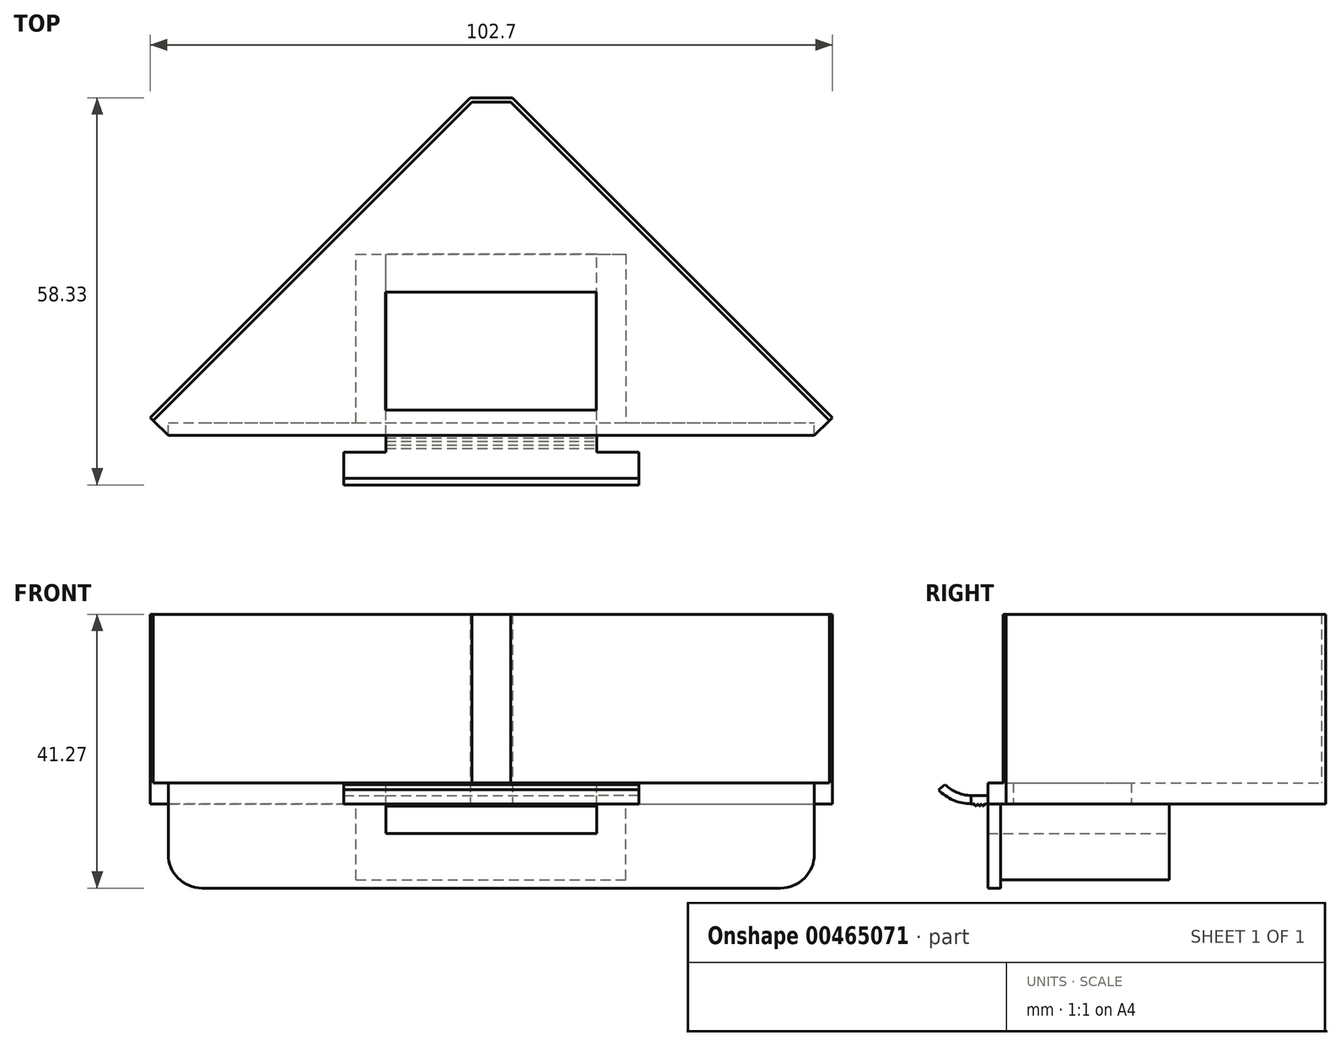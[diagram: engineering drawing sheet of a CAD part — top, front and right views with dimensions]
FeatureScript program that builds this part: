
annotation { "Feature Type Name" : "Feature", "Feature Type Description" : "" }
export const myFeature = defineFeature(function(context is Context, id is Id, definition is map)
    precondition{}
    {
        {
            var Q0;
            Q0=qCreatedBy(makeId("Top.planeOp"),FACE);
            var sketch = newSketch(context, id + "F0", { "sketchPlane" : qUnion([Q0])});
            skLineSegment(sketch, "E0", {"start": v(-3.17, 48.17) * mm, "end": v(-51.35, 0) * mm});
            skLineSegment(sketch, "E1", {"start": v(3.17, 48.17) * mm, "end": v(51.35, 0) * mm});
            skLineSegment(sketch, "E2", {"start": v(-51.35, 0) * mm, "end": v(51.35, 0) * mm, "construction": true});
            skLineSegment(sketch, "E3", {"start": v(3.17, 48.17) * mm, "end": v(-3.17, 48.17) * mm});
            skPoint(sketch, "E4.endSnap0", {"position": v(0, 0) * mm});
            skLineSegment(sketch, "E5", {"start": v(0, 0) * mm, "end": v(0, 48.17) * mm, "construction": true});
            skLineSegment(sketch, "E6", {"start": v(51.35, 0) * mm, "end": v(48.65, -2.7) * mm});
            skLineSegment(sketch, "E7", {"start": v(-51.35, 0) * mm, "end": v(-48.65, -2.7) * mm});
            skLineSegment(sketch, "E8", {"start": v(48.65, -2.7) * mm, "end": v(-48.65, -2.7) * mm});
            skSolve(sketch);
        }
        {
            var Q0;
            Q0=makeQuery(id+"F0.imprint","IMPRINT",FACE,{"disambiguationData":[TD([[makeQuery(id+"F0.imprint","IMPRINT",EDGE,{"derivedFrom":sQuery(id+"F0.wireOp",EDGE,"E0")}),1.0]])]});
            extrude(context, id + "F1", {"entities" : qUnion([Q0]), "depth" : 3.17 * mm, "offsetDistance" : 25.4 * mm});
        }
        {
            var Q0;
            Q0=makeQuery(id+"F1.opExtrude","CAP_FACE",FACE,{"disambiguationData":[OSD([sQuery(id+"F0.wireOp",EDGE,"E0"),sQuery(id+"F0.wireOp",EDGE,"E1"),sQuery(id+"F0.wireOp",EDGE,"E3"),sQuery(id+"F0.wireOp",EDGE,"E6"),sQuery(id+"F0.wireOp",EDGE,"E7"),sQuery(id+"F0.wireOp",EDGE,"E8")])],"isStart":false});
            var sketch = newSketch(context, id + "F2", { "sketchPlane" : qUnion([Q0])});
            skLineSegment(sketch, "E9", {"start": v(-51.35, 0) * mm, "end": v(-3.17, 48.17) * mm});
            skLineSegment(sketch, "E10", {"start": v(-3.17, 48.17) * mm, "end": v(3.17, 48.17) * mm});
            skLineSegment(sketch, "E11", {"start": v(3.17, 48.17) * mm, "end": v(51.35, 0) * mm});
            skLineSegment(sketch, "E12", {"start": v(51.35, 0) * mm, "end": v(50.9, -0.45) * mm});
            skLineSegment(sketch, "E13", {"start": v(-51.35, 0) * mm, "end": v(-50.9, -0.45) * mm});
            skLineSegment(sketch, "E14", {"start": v(-50.9, -0.45) * mm, "end": v(-2.92, 47.53) * mm});
            skLineSegment(sketch, "E15", {"start": v(50.9, -0.45) * mm, "end": v(2.92, 47.53) * mm});
            skLineSegment(sketch, "E16", {"start": v(-2.92, 47.53) * mm, "end": v(2.92, 47.53) * mm});
            skSolve(sketch);
        }
        {
            var Q0;
            Q0=makeQuery(id+"F2.imprint","IMPRINT",FACE,{"disambiguationData":[TD([[makeQuery(id+"F2.imprint","IMPRINT",EDGE,{"derivedFrom":sQuery(id+"F2.wireOp",EDGE,"E9")}),1.0]])]});
            extrude(context, id + "F3", {"entities" : qUnion([Q0]), "operationType" : NewBodyOperationType.ADD, "depth" : 25.4 * mm, "offsetDistance" : 25.4 * mm});
        }
        {
            var Q0;
            Q0=makeQuery(id+"F1.opExtrude","CAP_FACE",FACE,{"disambiguationData":[OSD([sQuery(id+"F0.wireOp",EDGE,"E0"),sQuery(id+"F0.wireOp",EDGE,"E1"),sQuery(id+"F0.wireOp",EDGE,"E3"),sQuery(id+"F0.wireOp",EDGE,"E6"),sQuery(id+"F0.wireOp",EDGE,"E7"),sQuery(id+"F0.wireOp",EDGE,"E8")])],"isStart":true});
            var sketch = newSketch(context, id + "F4", { "sketchPlane" : qUnion([Q0])});
            skLineSegment(sketch, "E17", {"start": v(-48.65, 2.7) * mm, "end": v(48.65, 2.7) * mm});
            skLineSegment(sketch, "E18", {"start": v(48.65, 2.7) * mm, "end": v(48.65, 0.79) * mm});
            skLineSegment(sketch, "E19", {"start": v(-48.65, 2.7) * mm, "end": v(-48.65, 0.79) * mm});
            skLineSegment(sketch, "E20", {"start": v(-48.65, 0.79) * mm, "end": v(48.65, 0.79) * mm});
            skSolve(sketch);
        }
        {
            var Q0;
            Q0=makeQuery(id+"F4.imprint","IMPRINT",FACE,{"disambiguationData":[TD([[makeQuery(id+"F4.imprint","IMPRINT",EDGE,{"derivedFrom":sQuery(id+"F4.wireOp",EDGE,"E17")}),1.0]])]});
            extrude(context, id + "F5", {"entities" : qUnion([Q0]), "operationType" : NewBodyOperationType.ADD, "depth" : 12.7 * mm, "offsetDistance" : 25.4 * mm});
        }
        {
            var Q0;
            Q0=makeQuery(id+"F1.opExtrude","CAP_FACE",FACE,{"disambiguationData":[OSD([sQuery(id+"F0.wireOp",EDGE,"E0"),sQuery(id+"F0.wireOp",EDGE,"E1"),sQuery(id+"F0.wireOp",EDGE,"E3"),sQuery(id+"F0.wireOp",EDGE,"E6"),sQuery(id+"F0.wireOp",EDGE,"E7"),sQuery(id+"F0.wireOp",EDGE,"E8")])],"isStart":true});
            var sketch = newSketch(context, id + "F6", { "sketchPlane" : qUnion([Q0])});
            skLineSegment(sketch, "E21", {"start": v(-20.36, 0.79) * mm, "end": v(-20.36, -24.61) * mm});
            skLineSegment(sketch, "E22", {"start": v(-20.36, -24.61) * mm, "end": v(20.28, -24.61) * mm});
            skLineSegment(sketch, "E23", {"start": v(20.28, -24.61) * mm, "end": v(20.28, 0.79) * mm});
            skLineSegment(sketch, "E24", {"start": v(20.28, 0.79) * mm, "end": v(-20.36, 0.79) * mm});
            skSolve(sketch);
        }
        {
            var Q0;
            Q0=makeQuery(id+"F6.imprint","IMPRINT",FACE,{"disambiguationData":[TD([[makeQuery(id+"F6.imprint","IMPRINT",EDGE,{"derivedFrom":sQuery(id+"F6.wireOp",EDGE,"E21")}),1.0]])]});
            extrude(context, id + "F7", {"entities" : qUnion([Q0]), "operationType" : NewBodyOperationType.ADD, "depth" : 11.43 * mm, "offsetDistance" : 25.4 * mm});
        }
        {
            var Q0;
            Q0=makeQuery(id+"F1.opExtrude","CAP_FACE",FACE,{"disambiguationData":[OSD([sQuery(id+"F0.wireOp",EDGE,"E0"),sQuery(id+"F0.wireOp",EDGE,"E1"),sQuery(id+"F0.wireOp",EDGE,"E3"),sQuery(id+"F0.wireOp",EDGE,"E6"),sQuery(id+"F0.wireOp",EDGE,"E7"),sQuery(id+"F0.wireOp",EDGE,"E8")])],"isStart":true});
            var sketch = newSketch(context, id + "F8", { "sketchPlane" : qUnion([Q0])});
            skLineSegment(sketch, "E25", {"start": v(15.84, -1.12) * mm, "end": v(-15.91, -1.12) * mm});
            skLineSegment(sketch, "E26", {"start": v(15.84, -1.12) * mm, "end": v(15.84, -18.9) * mm});
            skLineSegment(sketch, "E27", {"start": v(-15.91, -1.12) * mm, "end": v(-15.91, -18.9) * mm});
            skLineSegment(sketch, "E28", {"start": v(15.84, -18.9) * mm, "end": v(-15.91, -18.9) * mm});
            skSolve(sketch);
        }
        {
            var Q0;
            Q0=makeQuery(id+"F8.imprint","IMPRINT",FACE,{"disambiguationData":[TD([[makeQuery(id+"F8.imprint","IMPRINT",EDGE,{"derivedFrom":sQuery(id+"F8.wireOp",EDGE,"E25")}),1.0]])]});
            var Q1;
            Q1=makeQuery(id+"F1.opExtrude","CAP_FACE",FACE,{"disambiguationData":[OSD([sQuery(id+"F0.wireOp",EDGE,"E0"),sQuery(id+"F0.wireOp",EDGE,"E1"),sQuery(id+"F0.wireOp",EDGE,"E3"),sQuery(id+"F0.wireOp",EDGE,"E6"),sQuery(id+"F0.wireOp",EDGE,"E7"),sQuery(id+"F0.wireOp",EDGE,"E8")])],"isStart":false});
            extrude(context, id + "F9", {"entities" : qUnion([Q0]), "operationType" : NewBodyOperationType.REMOVE, "endBound" : BoundingType.UP_TO_SURFACE, "oppositeDirection" : true, "depth" : 25.4 * mm, "endBoundEntityFace" : qUnion([Q1]), "offsetDistance" : 25.4 * mm});
        }
        {
            var Q0;
            Q0=makeQuery(id+"F7.opExtrude","SWEPT_FACE",FACE,{"disambiguationData":[OSD([sQuery(id+"F6.wireOp",EDGE,"E22")])]});
            var sketch = newSketch(context, id + "F10", { "sketchPlane" : qUnion([Q0])});
            skLineSegment(sketch, "E29", {"start": v(0, 0) * mm, "end": v(0.04, -11.43) * mm, "construction": true});
            skLineSegment(sketch, "E30", {"start": v(-15.88, -4.44) * mm, "end": v(-15.88, 0) * mm});
            skLineSegment(sketch, "E31", {"start": v(-15.88, -4.44) * mm, "end": v(15.87, -4.44) * mm});
            skLineSegment(sketch, "E32", {"start": v(-15.88, 0) * mm, "end": v(15.87, 0) * mm});
            skLineSegment(sketch, "E33", {"start": v(15.87, -4.44) * mm, "end": v(15.87, 0) * mm});
            skSolve(sketch);
        }
        {
            var Q0;
            Q0=makeQuery(id+"F10.imprint","IMPRINT",FACE,{"disambiguationData":[TD([[makeQuery(id+"F10.imprint","IMPRINT",EDGE,{"derivedFrom":sQuery(id+"F10.wireOp",EDGE,"E30")}),-1.0]])]});
            var Q1;
            Q1=makeQuery(id+"F5.boolean.opBoolean","MERGE",FACE,{"derivedFrom":[makeQuery(id+"F1.opExtrude","SWEPT_FACE",FACE,{"disambiguationData":[OSD([sQuery(id+"F0.wireOp",EDGE,"E8")])]}),makeQuery(id+"F5.opExtrude","SWEPT_FACE",FACE,{"disambiguationData":[OSD([sQuery(id+"F4.wireOp",EDGE,"E17")])]})]});
            extrude(context, id + "F11", {"entities" : qUnion([Q0]), "operationType" : NewBodyOperationType.REMOVE, "endBound" : BoundingType.UP_TO_SURFACE, "oppositeDirection" : true, "depth" : 25.4 * mm, "endBoundEntityFace" : qUnion([Q1]), "offsetDistance" : 25.4 * mm});
        }
        {
            var Q0;
            Q0=makeQuery(id+"F5.boolean.opBoolean","MERGE",FACE,{"derivedFrom":[makeQuery(id+"F1.opExtrude","SWEPT_FACE",FACE,{"disambiguationData":[OSD([sQuery(id+"F0.wireOp",EDGE,"E8")])]}),makeQuery(id+"F5.opExtrude","SWEPT_FACE",FACE,{"disambiguationData":[OSD([sQuery(id+"F4.wireOp",EDGE,"E17")])]})]});
            var sketch = newSketch(context, id + "F12", { "sketchPlane" : qUnion([Q0])});
            skLineSegment(sketch, "E34", {"start": v(-15.87, 0) * mm, "end": v(15.88, 0) * mm});
            skLineSegment(sketch, "E35", {"start": v(15.88, 0) * mm, "end": v(15.88, 1.27) * mm});
            skLineSegment(sketch, "E36", {"start": v(-15.87, 0) * mm, "end": v(-15.87, 1.27) * mm});
            skLineSegment(sketch, "E37", {"start": v(-15.87, 1.27) * mm, "end": v(15.88, 1.27) * mm});
            skSolve(sketch);
        }
        {
            var Q0;
            Q0=makeQuery(id+"F12.imprint","IMPRINT",FACE,{"disambiguationData":[TD([[makeQuery(id+"F12.imprint","IMPRINT",EDGE,{"derivedFrom":sQuery(id+"F12.wireOp",EDGE,"E34")}),1.0]])]});
            extrude(context, id + "F13", {"entities" : qUnion([Q0]), "operationType" : NewBodyOperationType.ADD, "depth" : 2.54 * mm, "offsetDistance" : 25.4 * mm});
        }
        {
            var Q0;
            {var subQ0=sQuery(id+"F12.wireOp",EDGE,"E35");Q0=makeQuery(id+"Fu44CvdcrFSpyrk_1.boolean.opBoolean","MERGE",FACE,{"derivedFrom":[makeQuery(id+"F13.opExtrude","SWEPT_FACE",FACE,{"disambiguationData":[OSD([subQ0])]}),makeQuery(id+"Fu44CvdcrFSpyrk_1.opExtrude","CAP_FACE",FACE,{"disambiguationData":[OSD([subQ0,sQuery(id+"Fs8nSXfKUSs3tAb_1.wireOp",EDGE,"xyW1C8g9-NMOX-Sz8t-ZCwN-wzpP1ULmmn6w"),sQuery(id+"Fs8nSXfKUSs3tAb_1.wireOp",EDGE,"AC8nEQy7-J4ys-li4v-PORW-vjgA6UGfsqjF"),sQuery(id+"Fs8nSXfKUSs3tAb_1.wireOp",EDGE,"lg05YbEY-4m78-VyLW-hbrf-dj0eqnnLof9L")])],"isStart":true})]});}
            var sketch = newSketch(context, id + "F14", { "sketchPlane" : qUnion([Q0])});
            skLineSegment(sketch, "E38", {"start": v(-5.23, 1.27) * mm, "end": v(-5.23, 0) * mm, "construction": true});
            skLineSegment(sketch, "E39", {"start": v(-2.7, 0) * mm, "end": v(-2.7, 1.27) * mm, "construction": true});
            skLineSegment(sketch, "E40", {"start": v(-2.7, 1.27) * mm, "end": v(-5.23, 1.27) * mm, "construction": true});
            skLineSegment(sketch, "E41", {"start": v(-5.23, 0) * mm, "end": v(-2.7, 0) * mm, "construction": true});
            skLineSegment(sketch, "E42", {"start": v(-3.08, 0) * mm, "end": v(-3.6, -0.36) * mm});
            skLineSegment(sketch, "E43", {"start": v(-3.6, -0.36) * mm, "end": v(-3.6, 0) * mm});
            skLineSegment(sketch, "E44", {"start": v(-3.6, 0) * mm, "end": v(-3.08, 0) * mm});
            skLineSegment(sketch, "E45.1.0.0", {"start": v(-4.12, -0.36) * mm, "end": v(-4.12, 0) * mm});
            skLineSegment(sketch, "E45.1.0.1", {"start": v(-3.6, 0) * mm, "end": v(-4.12, -0.36) * mm});
            skLineSegment(sketch, "E45.2.0.0", {"start": v(-4.64, -0.36) * mm, "end": v(-4.64, 0) * mm});
            skLineSegment(sketch, "E45.2.0.1", {"start": v(-4.12, 0) * mm, "end": v(-4.64, -0.36) * mm});
            skLineSegment(sketch, "E45.direction1", {"start": v(-3.6, -0.36) * mm, "end": v(-4.12, -0.36) * mm, "construction": true});
            skSolve(sketch);
        }
        {
            var Q0;
            {var subQ0=sQuery(id+"F14.wireOp",EDGE,"E45.2.0.0");Q0=makeQuery(id+"F14.imprint","IMPRINT",FACE,{"disambiguationData":[TD([[makeQuery(id+"F14.imprint","IMPRINT",EDGE,{"derivedFrom":subQ0}),-1.0]])]});}
            var Q1;
            {var subQ0=sQuery(id+"F14.wireOp",EDGE,"E45.1.0.0");Q1=makeQuery(id+"F14.imprint","IMPRINT",FACE,{"disambiguationData":[TD([[makeQuery(id+"F14.imprint","IMPRINT",EDGE,{"derivedFrom":subQ0}),-1.0]])]});}
            var Q2;
            Q2=makeQuery(id+"F14.imprint","IMPRINT",FACE,{"disambiguationData":[TD([[makeQuery(id+"F14.imprint","IMPRINT",EDGE,{"derivedFrom":sQuery(id+"F14.wireOp",EDGE,"E42")}),-1.0]])]});
            var Q3;
            Q3=makeQuery(id+"F13.opExtrude","SWEPT_FACE",FACE,{"disambiguationData":[OSD([sQuery(id+"F12.wireOp",EDGE,"E36")])]});
            extrude(context, id + "F15", {"entities" : qUnion([Q0, Q1, Q2]), "operationType" : NewBodyOperationType.ADD, "endBound" : BoundingType.UP_TO_SURFACE, "oppositeDirection" : true, "depth" : 25.4 * mm, "endBoundEntityFace" : qUnion([Q3]), "offsetDistance" : 25.4 * mm});
        }
        {
            var Q0;
            {var subQ0=sQuery(id+"F12.wireOp",EDGE,"E35");var subQ1=sQuery(id+"F12.wireOp",EDGE,"E34");var subQ2=sQuery(id+"F10.wireOp",EDGE,"E30");var subQ3=sQuery(id+"F4.wireOp",EDGE,"E17");var subQ4=sQuery(id+"F0.wireOp",EDGE,"E8");Q0=makeQuery(id+"F15.boolean.opBoolean","MERGE",FACE,{"derivedFrom":[makeQuery(id+"F13.opExtrude","SWEPT_FACE",FACE,{"disambiguationData":[OSD([subQ0])]}),makeQuery(id+"F15.opExtrude","CAP_FACE",FACE,{"disambiguationData":[OSD([sQuery(id+"F14.wireOp",EDGE,"E42"),sQuery(id+"F14.wireOp",EDGE,"E43"),sQuery(id+"F14.wireOp",EDGE,"E44")])],"isStart":true}),makeQuery(id+"F15.opExtrude","CAP_FACE",FACE,{"disambiguationData":[OSD([subQ4,subQ3,subQ2,subQ1,subQ0,sQuery(id+"F14.wireOp",EDGE,"E45.1.0.0"),sQuery(id+"F14.wireOp",EDGE,"E45.1.0.1")])],"isStart":true}),makeQuery(id+"F15.opExtrude","CAP_FACE",FACE,{"disambiguationData":[OSD([subQ4,subQ3,subQ2,subQ1,subQ0,sQuery(id+"F14.wireOp",EDGE,"E45.2.0.0"),sQuery(id+"F14.wireOp",EDGE,"E45.2.0.1")])],"isStart":true})]});}
            var sketch = newSketch(context, id + "F16", { "sketchPlane" : qUnion([Q0])});
            skArc(sketch, "E46", {"start": v(-10.16, 2.12) * mm, "mid": v(-7.92, 0.55) * mm, "end": v(-5.23, 0) * mm});
            skArc(sketch, "E47", {"start": v(-9.16, 2.9) * mm, "mid": v(-7.36, 1.7) * mm, "end": v(-5.23, 1.27) * mm});
            skLineSegment(sketch, "E48", {"start": v(-10.16, 2.12) * mm, "end": v(-9.16, 2.9) * mm});
            skLineSegment(sketch, "E49", {"start": v(-5.23, 0) * mm, "end": v(-5.23, 1.27) * mm});
            skSolve(sketch);
        }
        {
            var Q0;
            Q0=makeQuery(id+"F16.imprint","IMPRINT",FACE,{"disambiguationData":[TD([[makeQuery(id+"F16.imprint","IMPRINT",EDGE,{"derivedFrom":sQuery(id+"F16.wireOp",EDGE,"E46")}),1.0]])]});
            extrude(context, id + "F17", {"entities" : qUnion([Q0]), "operationType" : NewBodyOperationType.ADD, "oppositeDirection" : true, "depth" : 38.1 * mm, "offsetDistance" : 25.4 * mm});
        }
        {
            var Q0;
            Q0=makeQuery(id+"F16.imprint","IMPRINT",FACE,{"disambiguationData":[TD([[makeQuery(id+"F16.imprint","IMPRINT",EDGE,{"derivedFrom":sQuery(id+"F16.wireOp",EDGE,"E46")}),1.0]])]});
            extrude(context, id + "F18", {"entities" : qUnion([Q0]), "operationType" : NewBodyOperationType.ADD, "depth" : 6.35 * mm, "offsetDistance" : 25.4 * mm});
        }
        {
            var Q0;
            Q0=makeQuery(id+"F5.opExtrude","CAP_EDGE",EDGE,{"disambiguationData":[OSD([sQuery(id+"F4.wireOp",EDGE,"E19")])],"isStart":false});
            var Q1;
            Q1=makeQuery(id+"F5.opExtrude","CAP_EDGE",EDGE,{"disambiguationData":[OSD([sQuery(id+"F4.wireOp",EDGE,"E18")])],"isStart":false});
            fillet(context, id + "F19", {"entities" : qUnion([Q0, Q1]), "radius" : 5.08 * mm, "tangentPropagation" : true, "allowEdgeOverflow" : false});
        }
    });
